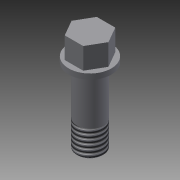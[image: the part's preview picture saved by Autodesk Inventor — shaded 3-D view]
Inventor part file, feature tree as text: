
AUTODESK INVENTOR PART (.ipt)
format: ipt  version: 2015 (Build 190159000, 159)  size: 98,304 bytes
history: native  units: mm
features: extrude x3, sketch x3, thread x1, chamfer x1
ambient origin geometry x8: Origin, YZ Plane, XZ Plane, XY Plane, X Axis, Y Axis, Z Axis, Center Point
bodies: 实体1 (feature_tree)
feature tree (8):
  extrude  "拉伸1"  Depth=1.0mm TaperAngle=0.0deg
  extrude  "拉伸2"  Depth=4.0mm TaperAngle=0.0deg
  extrude  "拉伸3"  Depth=14.0mm TaperAngle=0.0deg
  thread  "螺纹1"  [1 undecoded]
  chamfer  "倒角1"  Distance=0.25mm Angle=45.0deg
  sketch  "草图1"  dims[d0=8.0mm d1=1.0mm d2=0.0mm]
  sketch  "草图2"  dims[d3=6.0mm d4=4.0mm d5=0.0mm]
  sketch  "草图3"  dims[d6=5.0mm d7=14.0mm d8=0.0mm d9=5.0mm d10=0.0mm d11=0.25mm d12=2.0mm d13=45.0deg]
note: 1 required parameter value undecoded (feature->parameter linkage not recoverable at this tier; creation-order binding heuristic only, values carry confidence <= 0.55)
